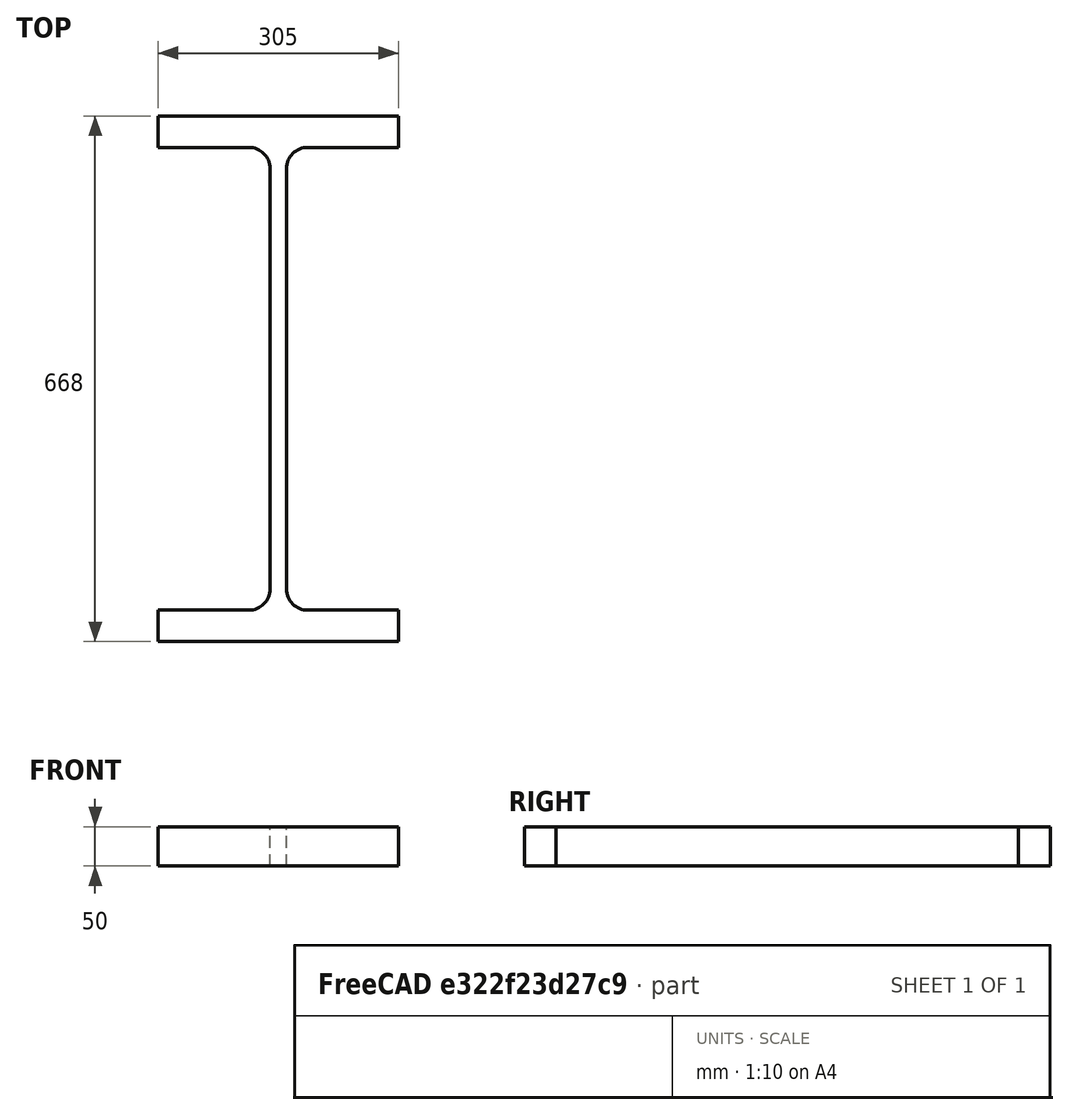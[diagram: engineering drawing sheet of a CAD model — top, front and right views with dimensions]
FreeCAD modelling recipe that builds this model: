
FCSTD DOCUMENT  (FreeCAD 0.15R4671 (Git))
Label: HE-M-Profile 650 DIN1025-4 S235JR
License: All rights reserved
LicenseURL: http://en.wikipedia.org/wiki/All_rights_reserved
objects: Sketcher::SketchObject×1, Part::Extrusion×1
note: 2 computed .brp shape members not serialized (recipe doc carries the construction recipe); baked Part::Feature solids carry a one-line shape summary decoded from their .brp

FEATURE [Sketcher::SketchObject] Sketch
  sketch-geometry (16):
    g0: LineSegment StartX=10.5 StartY=-267 StartZ=0 EndX=10.5 EndY=267 EndZ=0
    g1: LineSegment StartX=37.5 StartY=294 StartZ=0 EndX=152.5 EndY=294 EndZ=0
    g2: LineSegment StartX=152.5 StartY=294 StartZ=0 EndX=152.5 EndY=334 EndZ=0
    g3: LineSegment StartX=152.5 StartY=334 StartZ=0 EndX=-152.5 EndY=334 EndZ=0
    g4: LineSegment StartX=-152.5 StartY=334 StartZ=0 EndX=-152.5 EndY=294 EndZ=0
    g5: LineSegment StartX=-152.5 StartY=294 StartZ=0 EndX=-37.5 EndY=294 EndZ=0
    g6: LineSegment StartX=-10.5 StartY=267 StartZ=0 EndX=-10.5 EndY=-267 EndZ=0
    g7: LineSegment StartX=-37.5 StartY=-294 StartZ=0 EndX=-152.5 EndY=-294 EndZ=0
    g8: LineSegment StartX=-152.5 StartY=-294 StartZ=0 EndX=-152.5 EndY=-334 EndZ=0
    g9: LineSegment StartX=-152.5 StartY=-334 StartZ=0 EndX=152.5 EndY=-334 EndZ=0
    g10: LineSegment StartX=152.5 StartY=-334 StartZ=0 EndX=152.5 EndY=-294 EndZ=0
    g11: LineSegment StartX=152.5 StartY=-294 StartZ=0 EndX=37.5 EndY=-294 EndZ=0
    g12: ArcOfCircle CenterX=37.5 CenterY=267 CenterZ=0 NormalX=0 NormalY=0 NormalZ=1 Radius=27 StartAngle=1.5708 EndAngle=3.14159
    g13: ArcOfCircle CenterX=37.5 CenterY=-267 CenterZ=0 NormalX=0 NormalY=0 NormalZ=1 Radius=27 StartAngle=3.14159 EndAngle=4.71239
    g14: ArcOfCircle CenterX=-37.5 CenterY=267 CenterZ=0 NormalX=0 NormalY=0 NormalZ=1 Radius=27 StartAngle=0 EndAngle=1.5708
    g15: ArcOfCircle CenterX=-37.5 CenterY=-267 CenterZ=0 NormalX=0 NormalY=0 NormalZ=1 Radius=27 StartAngle=4.71239 EndAngle=6.28319
  constraints (42):
    c: Vertical(g0)
    c: Coincident(g2,g1)
    c: Vertical(g2)
    c: Coincident(g3,g2)
    c: Coincident(g4,g3)
    c: Vertical(g4)
    c: Coincident(g5,g4)
    c: Horizontal(g5)
    c: Vertical(g6)
    c: Horizontal(g7)
    c: Coincident(g8,g7)
    c: Vertical(g8)
    c: Coincident(g9,g8)
    c: Horizontal(g9)
    c: Coincident(g10,g9)
    c: Vertical(g10)
    c: Coincident(g11,g10)
    c: Horizontal(g11)
    c: Tangent(g1,g12) = 1.5708
    c: Tangent(g0,g12) = 1.5708
    c: Tangent(g0,g13) = 1.5708
    c: Tangent(g11,g13) = 1.5708
    c: Tangent(g5,g14) = 1.5708
    c: Tangent(g6,g14) = 1.5708
    c: Tangent(g6,g15) = 1.5708
    c: Tangent(g7,g15) = 1.5708
    c: Equal(g3,g9)
    c: Equal(g2,g4)
    c: Equal(g4,g8)
    c: Equal(g8,g10)
    c: Equal(g12,g14)
    c: Equal(g14,g15)
    c: Equal(g15,g13)
    c: Symmetric(g2,g3,g-2)
    c: Symmetric(g9,g8,g-2)
    c: Symmetric(g0,g6,g-2)
    c: Symmetric(g2,g9,g-1)
    c: DistanceY(g2,g9) = -668
    c: DistanceX(g3) = -305
    c: DistanceX(g0,g6) = -21
    c: DistanceY(g2) = 40
    c: Radius(g12) = 27
FEATURE [Part::Extrusion] Extrude  label="HE-M-Profile 650 DIN1025-4 S235JR"
  Base = -> Sketch
  Dir = (0,0,50)
  Solid = true
